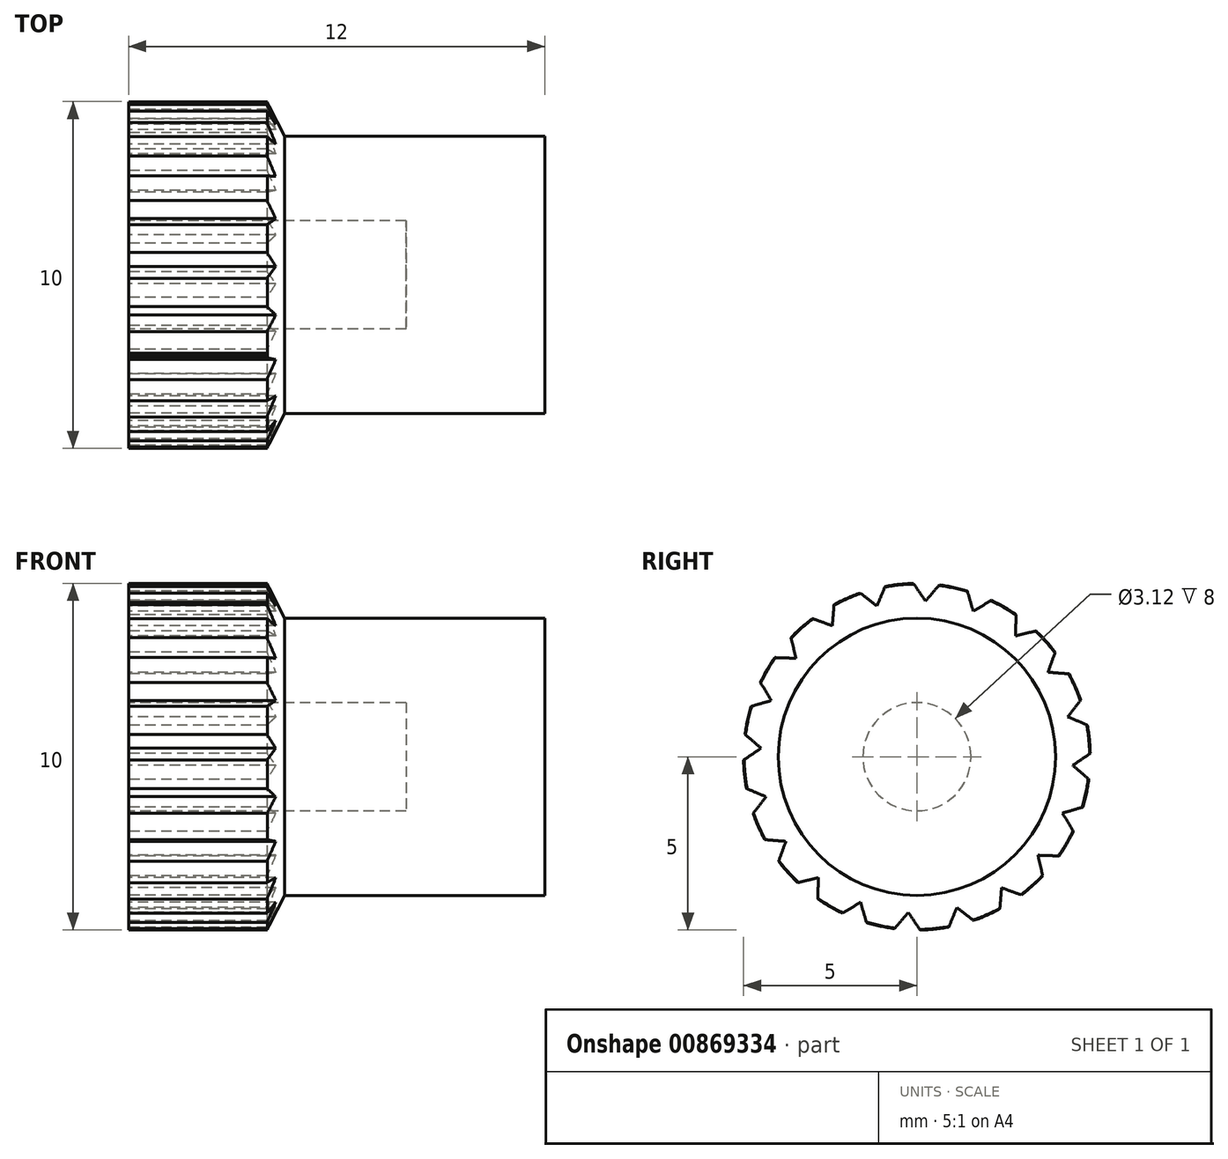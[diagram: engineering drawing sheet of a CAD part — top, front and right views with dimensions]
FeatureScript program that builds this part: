
annotation { "Feature Type Name" : "Feature", "Feature Type Description" : "" }
export const myFeature = defineFeature(function(context is Context, id is Id, definition is map)
    precondition{}
    {
        {
            var Q0;
            Q0=qCreatedBy(makeId("Right.planeOp"),FACE);
            var sketch = newSketch(context, id + "F0", { "sketchPlane" : qUnion([Q0])});
            skCircle(sketch, "E0", {"center": v(0, 0) * mm, "radius": 5 * mm});
            skSolve(sketch);
        }
        {
            var Q0;
            Q0=makeQuery(id+"F0.imprint","IMPRINT",FACE,{"disambiguationData":[TD([[makeQuery(id+"F0.imprint","IMPRINT",EDGE,{"derivedFrom":sQuery(id+"F0.wireOp",EDGE,"E0")}),1.0]])]});
            extrude(context, id + "F1", {"entities" : qUnion([Q0]), "depth" : 12 * mm, "offsetDistance" : 25 * mm});
        }
        {
            var Q0;
            Q0=makeQuery(id+"F1.opExtrude","CAP_FACE",FACE,{"disambiguationData":[OSD([sQuery(id+"F0.wireOp",EDGE,"E0")])],"isStart":true});
            var sketch = newSketch(context, id + "F2", { "sketchPlane" : qUnion([Q0])});
            skCircle(sketch, "E1", {"center": v(0, 0) * mm, "radius": 1.56 * mm});
            skSolve(sketch);
        }
        {
            var Q0;
            Q0=makeQuery(id+"F2.imprint","IMPRINT",FACE,{"disambiguationData":[TD([[makeQuery(id+"F2.imprint","IMPRINT",EDGE,{"derivedFrom":sQuery(id+"F2.wireOp",EDGE,"E1")}),1.0]])]});
            extrude(context, id + "F3", {"entities" : qUnion([Q0]), "operationType" : NewBodyOperationType.REMOVE, "oppositeDirection" : true, "depth" : 8 * mm, "offsetDistance" : 25 * mm});
        }
        {
            var Q0;
            Q0=qCreatedBy(makeId("Right.planeOp"),FACE);
            var sketch = newSketch(context, id + "F4", { "sketchPlane" : qUnion([Q0])});
            skCircle(sketch, "E2.0.0", {"center": v(0, 0) * mm, "radius": 5 * mm});
            skLineSegment(sketch, "E3", {"start": v(0, 0) * mm, "end": v(-2.7, 4.2) * mm, "construction": true});
            skLineSegment(sketch, "E4", {"start": v(-2.39, 4.4) * mm, "end": v(-2.44, 3.78) * mm});
            skLineSegment(sketch, "E5", {"start": v(-2.44, 3.78) * mm, "end": v(-3.02, 3.99) * mm});
            skArc(sketch, "E6", {"start": v(-2.89, 3.94) * mm, "mid": v(-3.01, 3.95) * mm, "end": v(-3.13, 3.9) * mm});
            skArc(sketch, "E7.MirrorCS", {"start": v(-2.4, 4.26) * mm, "mid": v(-2.36, 4.38) * mm, "end": v(-2.26, 4.46) * mm});
            skSolve(sketch);
        }
        {
            var Q0;
            {var subQ0=sQuery(id+"F4.wireOp",EDGE,"E4");Q0=makeQuery(id+"F4.imprint","IMPRINT",FACE,{"disambiguationData":[TD([[makeQuery(id+"F4.imprint","IMPRINT",EDGE,{"derivedFrom":subQ0}),-1.0]])]});}
            var Q1;
            {var subQ3=sQuery(id+"F4.wireOp",EDGE,"E6");Q1=makeQuery(id+"F4.imprint","IMPRINT",FACE,{"disambiguationData":[TD([[makeQuery(id+"F4.imprint","IMPRINT",EDGE,{"derivedFrom":subQ3}),-1.0]])]});}
            var Q2;
            {var subQ3=sQuery(id+"F4.wireOp",EDGE,"E7.MirrorCS");Q2=makeQuery(id+"F4.imprint","IMPRINT",FACE,{"disambiguationData":[TD([[makeQuery(id+"F4.imprint","IMPRINT",EDGE,{"derivedFrom":subQ3}),1.0]])]});}
            extrude(context, id + "F5", {"entities" : qUnion([Q0, Q1, Q2]), "depth" : 4 * mm, "offsetDistance" : 25 * mm});
        }
        {
            var Q0;
            Q0=makeQuery(id+"F5.opExtrude","SWEPT_BODY",BODY,{"disambiguationData":[OSD([sQuery(id+"F4.wireOp",EDGE,"E2.0.0"),sQuery(id+"F4.wireOp",EDGE,"E4"),sQuery(id+"F4.wireOp",EDGE,"E5")])]});
            var Q1;
            Q1=makeQuery(id+"F1.opExtrude","CAP_EDGE",EDGE,{"disambiguationData":[OSD([sQuery(id+"F0.wireOp",EDGE,"E0")])],"isStart":true});
            circularPattern(context, id + "F6", {"operationType" : NewBodyOperationType.REMOVE, "entities" : qUnion([Q0]), "axis" : qUnion([Q1]), "angle" : 360 * degree, "instanceCount" : 20, "equalSpace" : true});
        }
        {
            var Q0;
            Q0=makeQuery(id+"F1.opExtrude","CAP_FACE",FACE,{"disambiguationData":[OSD([sQuery(id+"F0.wireOp",EDGE,"E0")])],"isStart":false});
            var sketch = newSketch(context, id + "F7", { "sketchPlane" : qUnion([Q0])});
            skCircle(sketch, "E8.0.0", {"center": v(0, 0) * mm, "radius": 5 * mm});
            skCircle(sketch, "E9", {"center": v(0, 0) * mm, "radius": 4 * mm});
            skSolve(sketch);
        }
        {
            var Q0;
            Q0=makeQuery(id+"F7.imprint","IMPRINT",FACE,{"disambiguationData":[TD([[makeQuery(id+"F7.imprint","IMPRINT",EDGE,{"derivedFrom":sQuery(id+"F7.wireOp",EDGE,"E8.0.0")}),1.0]])]});
            extrude(context, id + "F8", {"entities" : qUnion([Q0]), "operationType" : NewBodyOperationType.REMOVE, "oppositeDirection" : true, "depth" : 8 * mm, "offsetDistance" : 25 * mm});
        }
        {
            var Q0;
            Q0=makeQuery(id+"F8.boolean.opBoolean","COPY",EDGE,{"derivedFrom":makeQuery(id+"F8.opExtrude","CAP_EDGE",EDGE,{"disambiguationData":[OSD([sQuery(id+"F7.wireOp",EDGE,"E9")])],"isStart":false})});
            chamfer(context, id + "F9", {"entities" : qUnion([Q0]), "chamferType" : ChamferType.OFFSET_ANGLE, "width" : 0.5 * mm, "oppositeDirection" : false, "angle" : 63 * degree, "tangentPropagation" : true});
        }
    });
